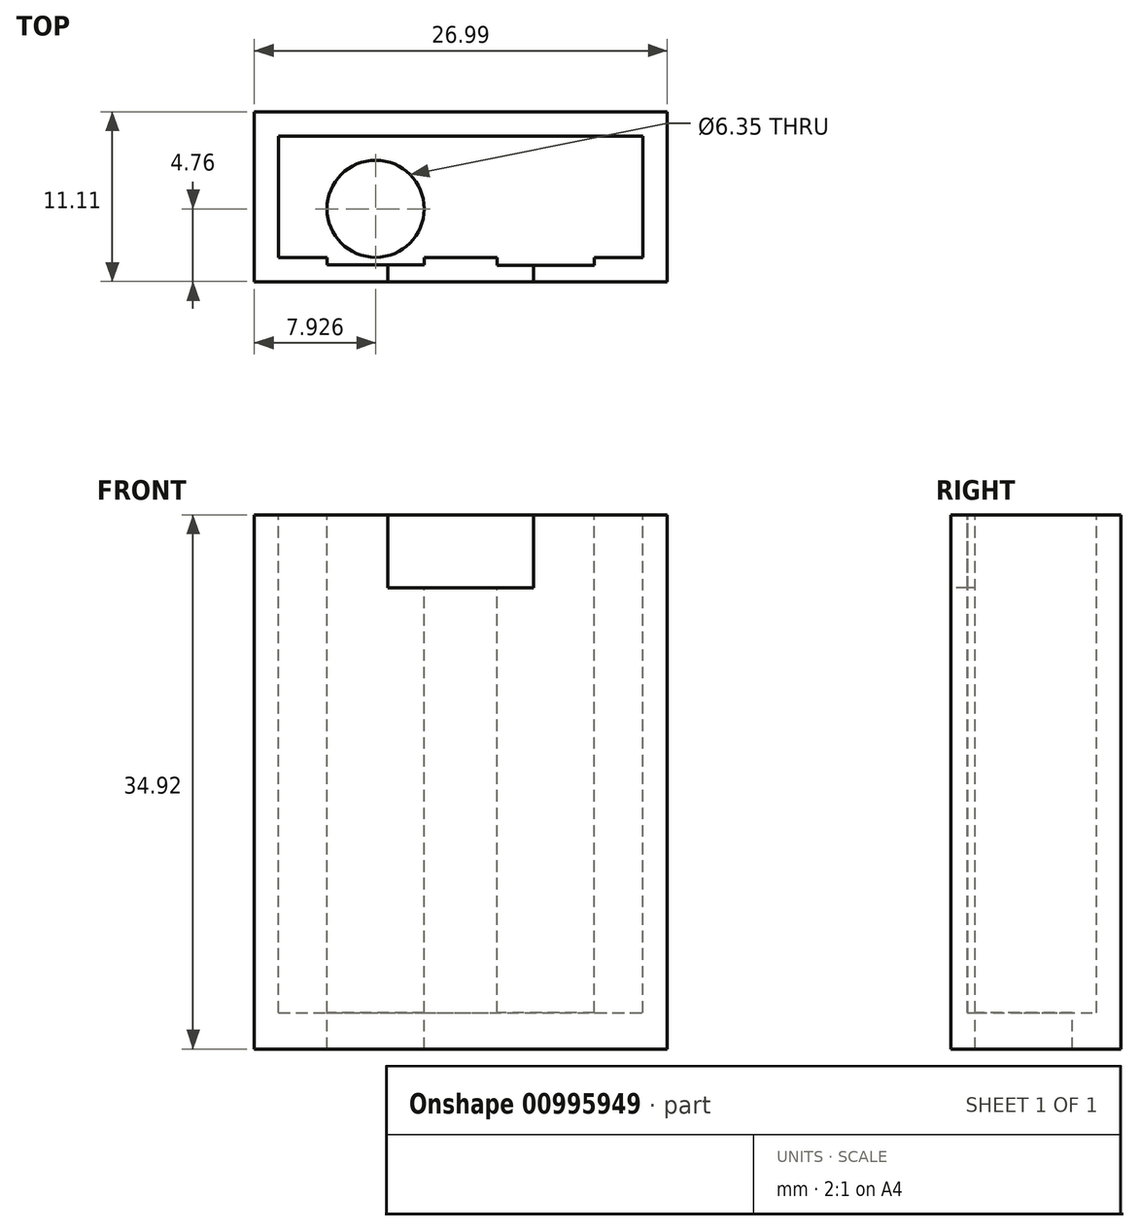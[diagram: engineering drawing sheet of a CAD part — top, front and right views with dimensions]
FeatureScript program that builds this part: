
annotation { "Feature Type Name" : "Feature", "Feature Type Description" : "" }
export const myFeature = defineFeature(function(context is Context, id is Id, definition is map)
    precondition{}
    {
        {
            var Q0;
            Q0=qCreatedBy(makeId("Front.planeOp"),FACE);
            var sketch = newSketch(context, id + "F0", { "sketchPlane" : qUnion([Q0])});
            skLineSegment(sketch, "E0", {"start": v(-42.37, 46.67) * mm, "end": v(-42.37, 11.75) * mm});
            skLineSegment(sketch, "E1", {"start": v(-42.37, 11.75) * mm, "end": v(-15.38, 11.75) * mm});
            skLineSegment(sketch, "E2", {"start": v(-15.38, 11.75) * mm, "end": v(-15.38, 46.67) * mm});
            skLineSegment(sketch, "E3", {"start": v(-15.38, 46.67) * mm, "end": v(-30.73, 46.67) * mm});
            skLineSegment(sketch, "E4", {"start": v(-30.73, 46.67) * mm, "end": v(-30.73, 46.67) * mm});
            skLineSegment(sketch, "E5", {"start": v(-30.73, 46.67) * mm, "end": v(-42.37, 46.67) * mm});
            skSolve(sketch);
        }
        {
            var Q0;
            Q0=makeQuery(id+"F0.imprint","IMPRINT",FACE,{"disambiguationData":[TD([[makeQuery(id+"F0.imprint","IMPRINT",EDGE,{"derivedFrom":sQuery(id+"F0.wireOp",EDGE,"E0")}),1.0]])]});
            extrude(context, id + "F1", {"entities" : qUnion([Q0]), "depth" : 11.1 * mm, "offsetDistance" : 25.4 * mm});
        }
        {
            var Q0;
            Q0=makeQuery(id+"F1.opExtrude","SWEPT_FACE",FACE,{"disambiguationData":[OSD([sQuery(id+"F0.wireOp",EDGE,"E3"),sQuery(id+"F0.wireOp",EDGE,"E5")])]});
            var sketch = newSketch(context, id + "F2", { "sketchPlane" : qUnion([Q0])});
            skLineSegment(sketch, "E6.0", {"start": v(-42.37, -1.59) * mm, "end": v(-15.38, -1.59) * mm});
            skLineSegment(sketch, "E7.0", {"start": v(-16.97, -11.11) * mm, "end": v(-16.97, 0) * mm});
            skLineSegment(sketch, "E8.0", {"start": v(-42.37, -9.53) * mm, "end": v(-15.38, -9.53) * mm});
            skLineSegment(sketch, "E9.0", {"start": v(-40.8, -11.11) * mm, "end": v(-40.8, 0) * mm});
            skLineSegment(sketch, "E10", {"start": v(-16.97, -1.59) * mm, "end": v(-20.14, -1.59) * mm});
            skLineSegment(sketch, "E11", {"start": v(-20.14, -9.53) * mm, "end": v(-20.14, -10.05) * mm});
            skLineSegment(sketch, "E12", {"start": v(-20.14, -10.05) * mm, "end": v(-26.5, -10.05) * mm});
            skLineSegment(sketch, "E13", {"start": v(-26.5, -10.05) * mm, "end": v(-26.5, -9.53) * mm});
            skLineSegment(sketch, "E14", {"start": v(-40.8, -9.53) * mm, "end": v(-37.62, -9.53) * mm});
            skLineSegment(sketch, "E15", {"start": v(-37.62, -9.53) * mm, "end": v(-37.62, -10.02) * mm});
            skLineSegment(sketch, "E16", {"start": v(-37.62, -10.02) * mm, "end": v(-31.27, -10.02) * mm});
            skLineSegment(sketch, "E17", {"start": v(-31.27, -10.02) * mm, "end": v(-31.27, -9.53) * mm});
            skSolve(sketch);
        }
        {
            var Q0;
            {var subQ5=sQuery(id+"F2.wireOp",EDGE,"E6.0");var subQ7=makeQuery(id+"F2.imprint","IMPRINT",VERTEX,{"derivedFrom":subQ5});Q0=makeQuery(id+"F2.imprint","IMPRINT",FACE,{"disambiguationData":[TD([[makeQuery(id+"F2.imprint","IMPRINT",EDGE,{"disambiguationData":[TD([[subQ7,1.0]])],"derivedFrom":subQ5}),-1.0]])]});}
            var Q1;
            {var subQ0=sQuery(id+"F2.wireOp",EDGE,"G1hrv64F-UfT7-tRS2-rPH5-RacdlyVmK1ax");Q1=makeQuery(id+"F2.imprint","IMPRINT",FACE,{"disambiguationData":[TD([[makeQuery(id+"F2.imprint","IMPRINT",EDGE,{"derivedFrom":subQ0}),1.0]])]});}
            var Q2;
            {var subQ0=sQuery(id+"F2.wireOp",EDGE,"E15");Q2=makeQuery(id+"F2.imprint","IMPRINT",FACE,{"disambiguationData":[TD([[makeQuery(id+"F2.imprint","IMPRINT",EDGE,{"derivedFrom":subQ0}),1.0]])]});}
            var Q3;
            {var subQ2=sQuery(id+"F2.wireOp",EDGE,"E11");Q3=makeQuery(id+"F2.imprint","IMPRINT",FACE,{"disambiguationData":[TD([[makeQuery(id+"F2.imprint","IMPRINT",EDGE,{"derivedFrom":subQ2}),-1.0]])]});}
            extrude(context, id + "F3", {"entities" : qUnion([Q0, Q1, Q2, Q3]), "operationType" : NewBodyOperationType.REMOVE, "oppositeDirection" : true, "depth" : 32.54 * mm, "offsetDistance" : 25.4 * mm});
        }
        {
            var Q0;
            Q0=makeQuery(id+"F3.boolean.opBoolean","COPY",FACE,{"derivedFrom":makeQuery(id+"F3.opExtrude","CAP_FACE",FACE,{"disambiguationData":[OSD([sQuery(id+"F2.wireOp",EDGE,"E6.0"),sQuery(id+"F2.wireOp",EDGE,"E7.0"),sQuery(id+"F2.wireOp",EDGE,"E8.0"),sQuery(id+"F2.wireOp",EDGE,"E9.0"),sQuery(id+"F2.wireOp",EDGE,"E11"),sQuery(id+"F2.wireOp",EDGE,"E12"),sQuery(id+"F2.wireOp",EDGE,"E13"),sQuery(id+"F2.wireOp",EDGE,"E15"),sQuery(id+"F2.wireOp",EDGE,"E16"),sQuery(id+"F2.wireOp",EDGE,"E17")])],"isStart":false})});
            var sketch = newSketch(context, id + "F4", { "sketchPlane" : qUnion([Q0])});
            skLineSegment(sketch, "E18", {"start": v(-34.44, -9.53) * mm, "end": v(-34.44, -6.35) * mm});
            skPoint(sketch, "E18.startSnap0", {"position": v(-34.44, -10.02) * mm});
            skCircle(sketch, "E19", {"center": v(-34.44, -6.35) * mm, "radius": 3.18 * mm});
            skSolve(sketch);
        }
        {
            var Q0;
            Q0=makeQuery(id+"F4.imprint","IMPRINT",FACE,{"disambiguationData":[TD([[makeQuery(id+"F4.imprint","IMPRINT",EDGE,{"derivedFrom":sQuery(id+"F4.wireOp",EDGE,"E19")}),1.0]])]});
            extrude(context, id + "F5", {"entities" : qUnion([Q0]), "operationType" : NewBodyOperationType.REMOVE, "endBound" : BoundingType.THROUGH_ALL, "oppositeDirection" : true, "depth" : 25.4 * mm, "offsetDistance" : 25.4 * mm});
        }
        {
            var Q0;
            Q0=makeQuery(id+"F1.opExtrude","CAP_FACE",FACE,{"disambiguationData":[OSD([sQuery(id+"F0.wireOp",EDGE,"E0"),sQuery(id+"F0.wireOp",EDGE,"E1"),sQuery(id+"F0.wireOp",EDGE,"E2"),sQuery(id+"F0.wireOp",EDGE,"E3"),sQuery(id+"F0.wireOp",EDGE,"E5")])],"isStart":false});
            var sketch = newSketch(context, id + "F6", { "sketchPlane" : qUnion([Q0])});
            skLineSegment(sketch, "E20", {"start": v(-24.11, 46.67) * mm, "end": v(-24.11, 41.91) * mm});
            skLineSegment(sketch, "E21", {"start": v(-24.11, 41.91) * mm, "end": v(-33.64, 41.91) * mm});
            skLineSegment(sketch, "E22", {"start": v(-33.64, 41.91) * mm, "end": v(-33.64, 46.67) * mm});
            skSolve(sketch);
        }
        {
            var Q0;
            {var subQ0=sQuery(id+"F6.wireOp",EDGE,"E20");Q0=makeQuery(id+"F6.imprint","IMPRINT",FACE,{"disambiguationData":[TD([[makeQuery(id+"F6.imprint","IMPRINT",EDGE,{"derivedFrom":subQ0}),-1.0]])]});}
            extrude(context, id + "F7", {"entities" : qUnion([Q0]), "operationType" : NewBodyOperationType.REMOVE, "oppositeDirection" : true, "depth" : 3.17 * mm, "offsetDistance" : 25.4 * mm});
        }
    });
